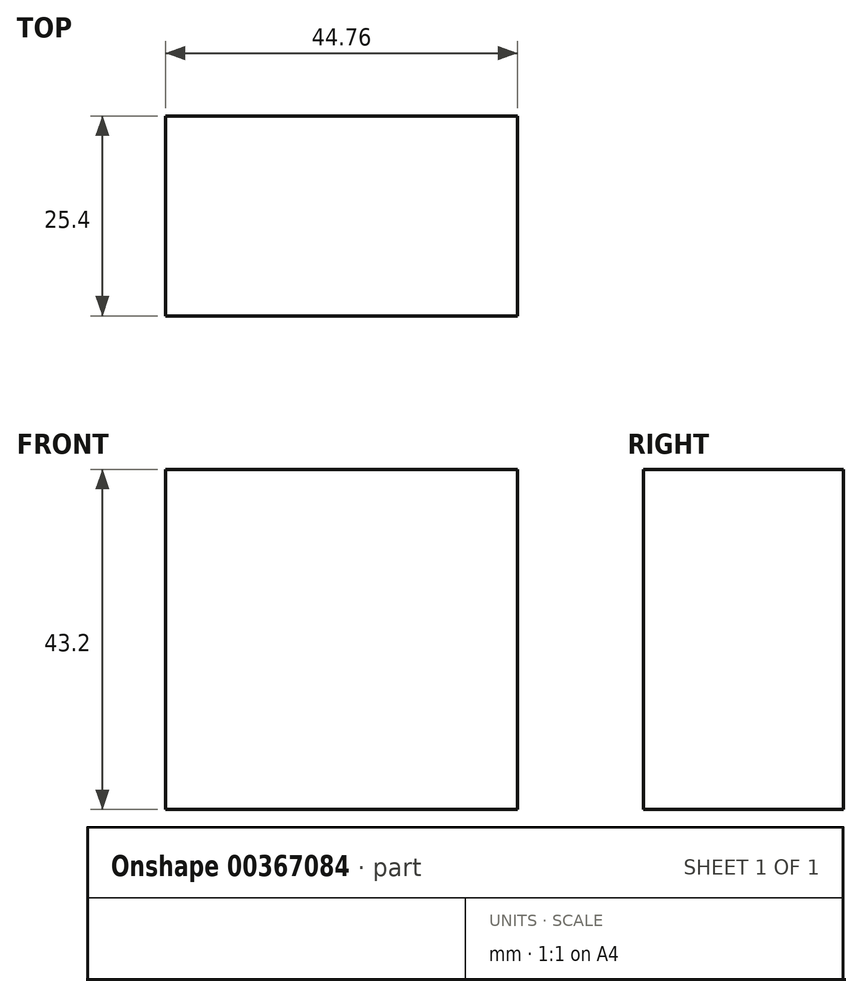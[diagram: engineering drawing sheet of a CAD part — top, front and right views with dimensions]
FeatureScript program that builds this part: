
annotation { "Feature Type Name" : "Feature", "Feature Type Description" : "" }
export const myFeature = defineFeature(function(context is Context, id is Id, definition is map)
    precondition{}
    {
        {
            var Q0;
            Q0=qCreatedBy(makeId("Front.planeOp"),FACE);
            var sketch = newSketch(context, id + "F0", { "sketchPlane" : qUnion([Q0])});
            skLineSegment(sketch, "E0", {"start": v(0, 0) * mm, "end": v(0, 43.2) * mm});
            skLineSegment(sketch, "E1", {"start": v(0, 43.2) * mm, "end": v(44.76, 43.2) * mm});
            skLineSegment(sketch, "E2", {"start": v(44.76, 43.2) * mm, "end": v(44.76, 0) * mm});
            skLineSegment(sketch, "E3", {"start": v(44.76, 0) * mm, "end": v(0, 0) * mm});
            skSolve(sketch);
        }
        {
            var Q0;
            Q0=makeQuery(id+"F0.imprint","IMPRINT",FACE,{"disambiguationData":[TD([[makeQuery(id+"F0.imprint","IMPRINT",EDGE,{"derivedFrom":sQuery(id+"F0.wireOp",EDGE,"E0")}),-1.0]])]});
            extrude(context, id + "F1", {"entities" : qUnion([Q0]), "depth" : 25.4 * mm});
        }
    });
